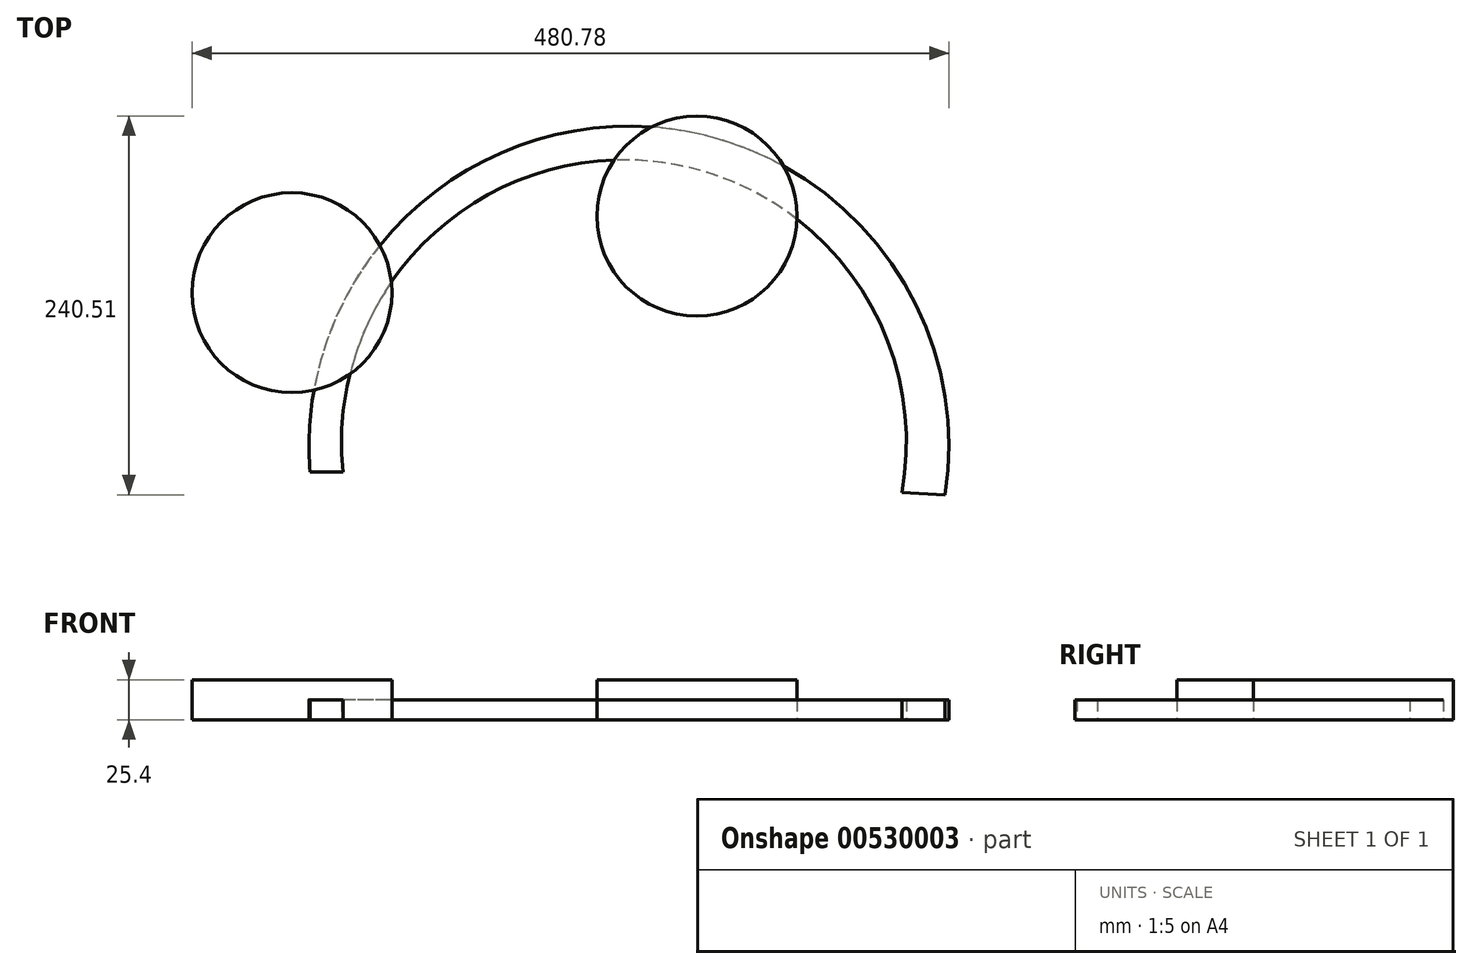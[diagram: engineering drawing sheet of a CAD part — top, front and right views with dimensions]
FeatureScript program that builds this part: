
annotation { "Feature Type Name" : "Feature", "Feature Type Description" : "" }
export const myFeature = defineFeature(function(context is Context, id is Id, definition is map)
    precondition{}
    {
        {
            var Q0;
            Q0=qCreatedBy(makeId("Top.planeOp"),FACE);
            var sketch = newSketch(context, id + "F0", { "sketchPlane" : qUnion([Q0])});
            skCircle(sketch, "E0", {"center": v(-225.25, -12.12) * mm, "radius": 63.5 * mm});
            skCircle(sketch, "E1", {"center": v(31.97, 36.58) * mm, "radius": 63.5 * mm});
            skSolve(sketch);
        }
        {
            var Q0;
            Q0=makeQuery(id+"F0.imprint","IMPRINT",FACE,{"disambiguationData":[TD([[makeQuery(id+"F0.imprint","IMPRINT",EDGE,{"derivedFrom":sQuery(id+"F0.wireOp",EDGE,"E0")}),1.0]])]});
            var Q1;
            Q1=makeQuery(id+"F0.imprint","IMPRINT",FACE,{"disambiguationData":[TD([[makeQuery(id+"F0.imprint","IMPRINT",EDGE,{"derivedFrom":sQuery(id+"F0.wireOp",EDGE,"E1")}),1.0]])]});
            extrude(context, id + "F1", {"entities" : qUnion([Q0, Q1]), "depth" : 25.4 * mm, "offsetDistance" : 25.4 * mm});
        }
        {
            var Q0;
            Q0=qCreatedBy(makeId("Top.planeOp"),FACE);
            var sketch = newSketch(context, id + "F2", { "sketchPlane" : qUnion([Q0])});
            skArc(sketch, "E2", {"start": v(189.67, -140.43) * mm, "mid": v(-3.91, 93.53) * mm, "end": v(-213.7, -126.02) * mm});
            skArc(sketch, "E3", {"start": v(162.17, -139.12) * mm, "mid": v(-7.73, 72.17) * mm, "end": v(-192.74, -126.02) * mm});
            skLineSegment(sketch, "E4", {"start": v(-213.7, -126.02) * mm, "end": v(-192.74, -126.02) * mm});
            skLineSegment(sketch, "E5", {"start": v(162.17, -139.12) * mm, "end": v(189.67, -140.43) * mm});
            skSolve(sketch);
        }
        {
            var Q0;
            Q0=makeQuery(id+"F2.imprint","IMPRINT",FACE,{"disambiguationData":[TD([[makeQuery(id+"F2.imprint","IMPRINT",EDGE,{"derivedFrom":sQuery(id+"F2.wireOp",EDGE,"E2")}),1.0]])]});
            extrude(context, id + "F3", {"entities" : qUnion([Q0]), "depth" : 12.7 * mm, "offsetDistance" : 25.4 * mm});
        }
        {
            var Q0;
            Q0=makeQuery(id+"F0.imprint","IMPRINT",FACE,{"disambiguationData":[TD([[makeQuery(id+"F0.imprint","IMPRINT",EDGE,{"derivedFrom":sQuery(id+"F0.wireOp",EDGE,"E0")}),1.0]])]});
            var Q1;
            Q1=makeQuery(id+"F0.imprint","IMPRINT",FACE,{"disambiguationData":[TD([[makeQuery(id+"F0.imprint","IMPRINT",EDGE,{"derivedFrom":sQuery(id+"F0.wireOp",EDGE,"E1")}),1.0]])]});
            extrude(context, id + "F4", {"entities" : qUnion([Q0, Q1]), "depth" : 25.4 * mm, "offsetDistance" : 25.4 * mm});
        }
    });
